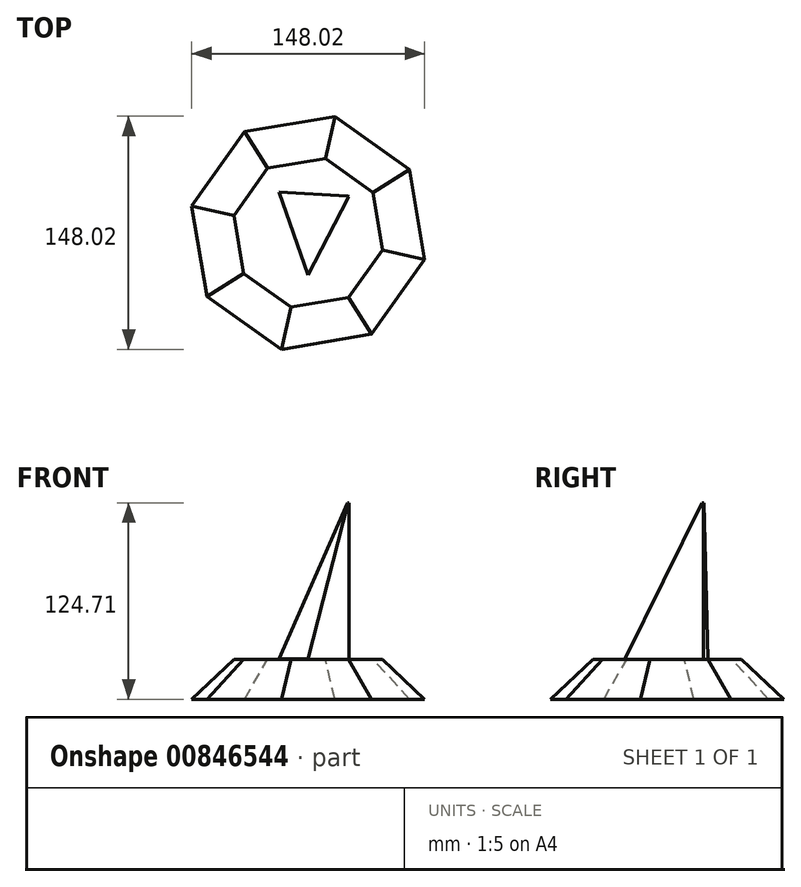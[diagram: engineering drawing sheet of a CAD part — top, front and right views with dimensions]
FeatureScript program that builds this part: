
annotation { "Feature Type Name" : "Feature", "Feature Type Description" : "" }
export const myFeature = defineFeature(function(context is Context, id is Id, definition is map)
    precondition{}
    {
        {
            var Q0;
            Q0=qCreatedBy(makeId("Top.planeOp"),FACE);
            var sketch = newSketch(context, id + "F0", { "sketchPlane" : qUnion([Q0])});
            skCircle(sketch, "E0.cCircle", {"center": v(0, 0) * mm, "radius": 70.15 * mm, "construction": true});
            skLineSegment(sketch, "E0.0", {"start": v(74, -16.98) * mm, "end": v(40.32, -64.34) * mm});
            skLineSegment(sketch, "E0.1", {"start": v(40.32, -64.34) * mm, "end": v(-16.98, -74) * mm});
            skLineSegment(sketch, "E0.2", {"start": v(-16.98, -74) * mm, "end": v(-64.34, -40.32) * mm});
            skLineSegment(sketch, "E0.3", {"start": v(-64.34, -40.32) * mm, "end": v(-74, 16.98) * mm});
            skLineSegment(sketch, "E0.4", {"start": v(-74, 16.98) * mm, "end": v(-40.32, 64.34) * mm});
            skLineSegment(sketch, "E0.5", {"start": v(-40.32, 64.34) * mm, "end": v(16.98, 74) * mm});
            skLineSegment(sketch, "E0.6", {"start": v(16.98, 74) * mm, "end": v(64.34, 40.32) * mm});
            skLineSegment(sketch, "E0.7", {"start": v(64.34, 40.32) * mm, "end": v(74, -16.98) * mm});
            skPoint(sketch, "E0.0.midPoint", {"position": v(57.16, -40.66) * mm});
            skSolve(sketch);
        }
        {
            var Q0;
            Q0=makeQuery(id+"F0.imprint","IMPRINT",FACE,{"disambiguationData":[TD([[makeQuery(id+"F0.imprint","IMPRINT",EDGE,{"derivedFrom":sQuery(id+"F0.wireOp",EDGE,"E0.0")}),-1.0]])]});
            extrude(context, id + "F1", {"entities" : qUnion([Q0]), "depth" : 25.4 * mm, "offsetDistance" : 25.4 * mm});
        }
        {
            var Q0;
            Q0=makeQuery(id+"F1.opExtrude","CAP_EDGE",EDGE,{"disambiguationData":[OSD([sQuery(id+"F0.wireOp",EDGE,"E0.1")])],"isStart":false});
            var Q1;
            Q1=makeQuery(id+"F1.opExtrude","CAP_EDGE",EDGE,{"disambiguationData":[OSD([sQuery(id+"F0.wireOp",EDGE,"E0.0")])],"isStart":false});
            var Q2;
            Q2=makeQuery(id+"F1.opExtrude","CAP_EDGE",EDGE,{"disambiguationData":[OSD([sQuery(id+"F0.wireOp",EDGE,"E0.7")])],"isStart":false});
            var Q3;
            Q3=makeQuery(id+"F1.opExtrude","CAP_EDGE",EDGE,{"disambiguationData":[OSD([sQuery(id+"F0.wireOp",EDGE,"E0.6")])],"isStart":false});
            var Q4;
            Q4=makeQuery(id+"F1.opExtrude","CAP_EDGE",EDGE,{"disambiguationData":[OSD([sQuery(id+"F0.wireOp",EDGE,"E0.5")])],"isStart":false});
            var Q5;
            Q5=makeQuery(id+"F1.opExtrude","CAP_EDGE",EDGE,{"disambiguationData":[OSD([sQuery(id+"F0.wireOp",EDGE,"E0.3")])],"isStart":false});
            var Q6;
            Q6=makeQuery(id+"F1.opExtrude","CAP_EDGE",EDGE,{"disambiguationData":[OSD([sQuery(id+"F0.wireOp",EDGE,"E0.2")])],"isStart":false});
            var Q7;
            Q7=makeQuery(id+"F1.opExtrude","CAP_EDGE",EDGE,{"disambiguationData":[OSD([sQuery(id+"F0.wireOp",EDGE,"E0.4")])],"isStart":false});
            chamfer(context, id + "F2", {"entities" : qUnion([Q0, Q1, Q2, Q3, Q4, Q5, Q6, Q7]), "width" : 25.4 * mm, "tangentPropagation" : true});
        }
        {
            var Q0;
            Q0=makeQuery(id+"F1.opExtrude","CAP_FACE",FACE,{"disambiguationData":[OSD([sQuery(id+"F0.wireOp",EDGE,"E0.0"),sQuery(id+"F0.wireOp",EDGE,"E0.1"),sQuery(id+"F0.wireOp",EDGE,"E0.2"),sQuery(id+"F0.wireOp",EDGE,"E0.3"),sQuery(id+"F0.wireOp",EDGE,"E0.4"),sQuery(id+"F0.wireOp",EDGE,"E0.5"),sQuery(id+"F0.wireOp",EDGE,"E0.6"),sQuery(id+"F0.wireOp",EDGE,"E0.7")])],"isStart":false});
            var sketch = newSketch(context, id + "F3", { "sketchPlane" : qUnion([Q0])});
            skLineSegment(sketch, "E1", {"start": v(0, -26.7) * mm, "end": v(25.94, 23.15) * mm});
            skPoint(sketch, "E1.endSnap0", {"position": v(25.94, 36.47) * mm});
            skLineSegment(sketch, "E2", {"start": v(25.94, 23.15) * mm, "end": v(-18.64, 25.94) * mm});
            skPoint(sketch, "E2.endSnap0", {"position": v(-36.47, 25.94) * mm});
            skLineSegment(sketch, "E3", {"start": v(-18.64, 25.94) * mm, "end": v(0, -26.7) * mm});
            skSolve(sketch);
        }
        {
            var Q0;
            Q0=makeQuery(id+"F3.imprint","IMPRINT",FACE,{"disambiguationData":[TD([[makeQuery(id+"F3.imprint","IMPRINT",EDGE,{"derivedFrom":sQuery(id+"F3.wireOp",EDGE,"E1")}),1.0]])]});
            extrude(context, id + "F4", {"entities" : qUnion([Q0]), "operationType" : NewBodyOperationType.ADD, "depth" : 99.31 * mm, "offsetDistance" : 25.4 * mm});
        }
        {
            var Q0;
            Q0=makeQuery(id+"F4.opExtrude","CAP_EDGE",EDGE,{"disambiguationData":[OSD([sQuery(id+"F3.wireOp",EDGE,"E3")])],"isStart":false});
            chamfer(context, id + "F5", {"entities" : qUnion([Q0]), "chamferType" : ChamferType.OFFSET_ANGLE, "width" : 40.1 * mm, "oppositeDirection" : false, "angle" : 68 * degree, "tangentPropagation" : true});
        }
    });
